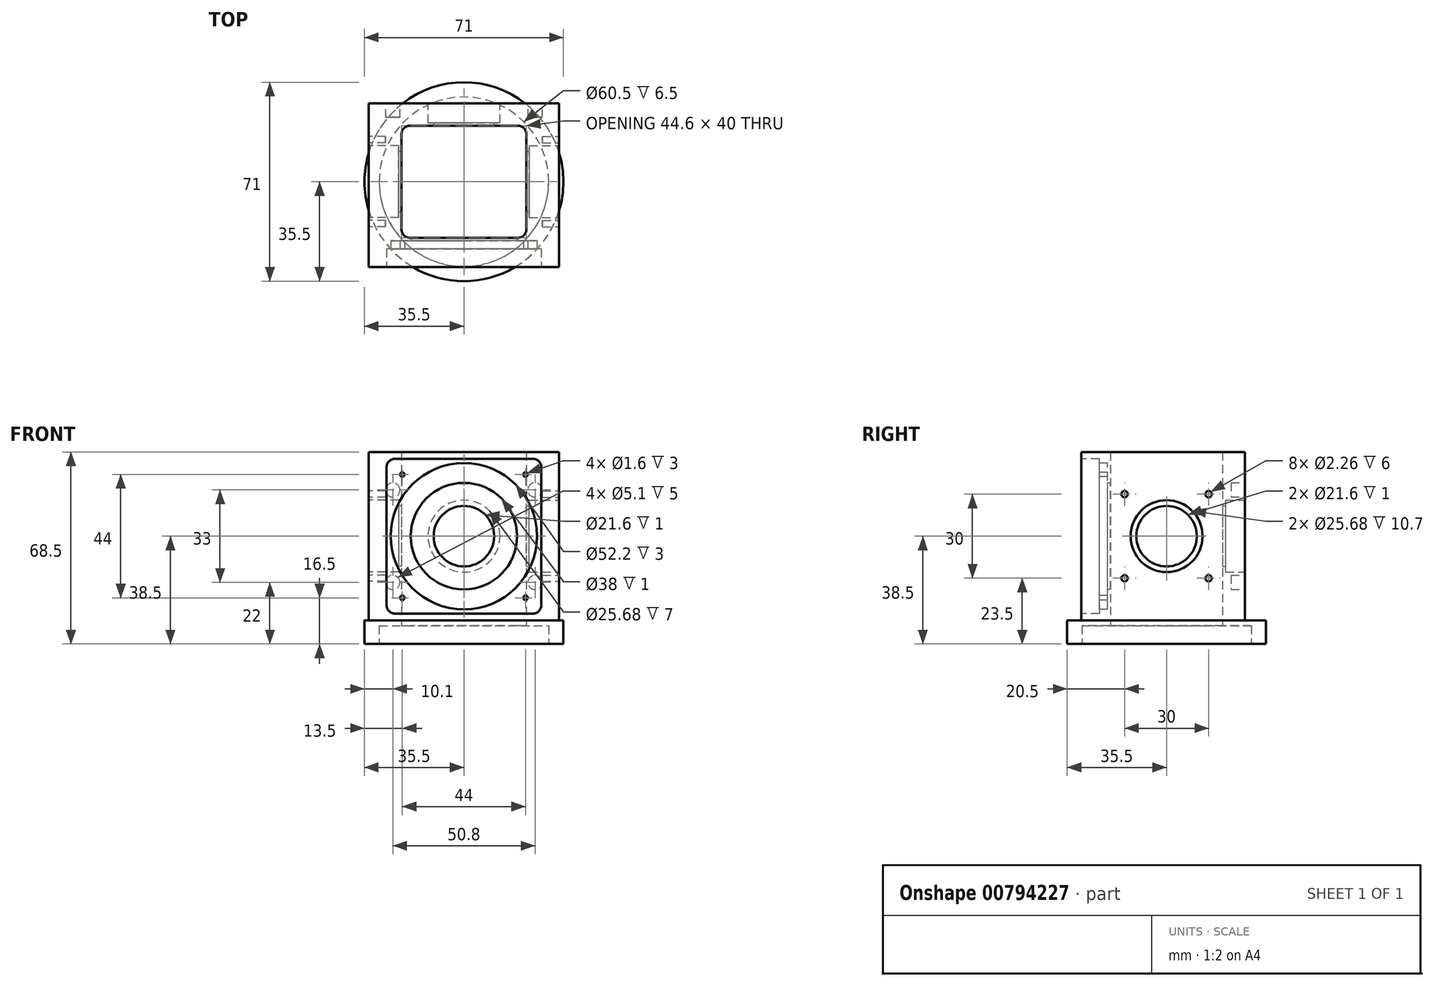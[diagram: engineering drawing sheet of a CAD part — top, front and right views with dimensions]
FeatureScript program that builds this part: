
annotation { "Feature Type Name" : "Feature", "Feature Type Description" : "" }
export const myFeature = defineFeature(function(context is Context, id is Id, definition is map)
    precondition{}
    {
        {
            var Q0;
            Q0=qCreatedBy(makeId("Top.planeOp"),FACE);
            var sketch = newSketch(context, id + "F0", { "sketchPlane" : qUnion([Q0])});
            skCircle(sketch, "E0", {"center": v(0, 0) * mm, "radius": 30.25 * mm});
            skSolve(sketch);
        }
        {
            var Q0;
            Q0=qCreatedBy(makeId("Top.planeOp"),FACE);
            var sketch = newSketch(context, id + "F1", { "sketchPlane" : qUnion([Q0])});
            skCircle(sketch, "E1", {"center": v(0, 0) * mm, "radius": 35.5 * mm});
            skSolve(sketch);
        }
        {
            var Q0;
            Q0=qSketchRegion(id+"F1",true);
            extrude(context, id + "F2", {"entities" : qUnion([Q0]), "depth" : 8.5 * mm, "offsetDistance" : 25 * mm});
        }
        {
            var Q0;
            Q0=qSketchRegion(id+"F0",true);
            extrude(context, id + "F3", {"entities" : qUnion([Q0]), "operationType" : NewBodyOperationType.REMOVE, "depth" : 8.5 * mm, "offsetDistance" : 25 * mm});
        }
        {
            var Q0;
            Q0=makeQuery(id+"F2.opExtrude","CAP_FACE",FACE,{"disambiguationData":[OSD([sQuery(id+"F1.wireOp",EDGE,"E1")])],"isStart":false});
            var sketch = newSketch(context, id + "F4", { "sketchPlane" : qUnion([Q0])});
            skLineSegment(sketch, "E2.bottom", {"start": v(19.3, -20) * mm, "end": v(-19.3, -20) * mm});
            skLineSegment(sketch, "E2.top", {"start": v(19.3, 20) * mm, "end": v(-19.3, 20) * mm});
            skLineSegment(sketch, "E2.left", {"start": v(22.3, -17) * mm, "end": v(22.3, 17) * mm});
            skLineSegment(sketch, "E2.right", {"start": v(-22.3, -17) * mm, "end": v(-22.3, 17) * mm});
            skPoint(sketch, "E2.middle", {"position": v(0, 0) * mm});
            skPoint(sketch, "E3.visualSharp", {"position": v(-22.3, 20) * mm});
            skArc(sketch, "E3.filletArc", {"start": v(-19.3, 20) * mm, "mid": v(-21.42, 19.12) * mm, "end": v(-22.3, 17) * mm});
            skPoint(sketch, "E4.visualSharp", {"position": v(22.3, 20) * mm});
            skArc(sketch, "E4.filletArc", {"start": v(22.3, 17) * mm, "mid": v(21.42, 19.12) * mm, "end": v(19.3, 20) * mm});
            skPoint(sketch, "E5.visualSharp", {"position": v(22.3, -20) * mm});
            skArc(sketch, "E5.filletArc", {"start": v(19.3, -20) * mm, "mid": v(21.42, -19.12) * mm, "end": v(22.3, -17) * mm});
            skPoint(sketch, "E6.visualSharp", {"position": v(-22.3, -20) * mm});
            skArc(sketch, "E6.filletArc", {"start": v(-22.3, -17) * mm, "mid": v(-21.42, -19.12) * mm, "end": v(-19.3, -20) * mm});
            skSolve(sketch);
        }
        {
            var Q0;
            Q0=makeQuery(id+"F4.imprint","IMPRINT",FACE,{"disambiguationData":[TD([[makeQuery(id+"F4.imprint","IMPRINT",EDGE,{"derivedFrom":makeQuery(id+"F2.opExtrude","CAP_EDGE",EDGE,{"disambiguationData":[OSD([sQuery(id+"F1.wireOp",EDGE,"E1")])],"isStart":false})}),1.0]])]});
            var sketch = newSketch(context, id + "F5", { "sketchPlane" : qUnion([Q0])});
            skLineSegment(sketch, "E7.bottom", {"start": v(-34, 0) * mm, "end": v(34, 0) * mm});
            skLineSegment(sketch, "E7.top", {"start": v(-34, 28) * mm, "end": v(34, 28) * mm});
            skLineSegment(sketch, "E7.left", {"start": v(-34, 0) * mm, "end": v(-34, 28) * mm});
            skLineSegment(sketch, "E7.right", {"start": v(34, 0) * mm, "end": v(34, 28) * mm});
            skLineSegment(sketch, "E8.top", {"start": v(-34, -30.5) * mm, "end": v(34, -30.5) * mm});
            skLineSegment(sketch, "E8.left", {"start": v(-34, 0) * mm, "end": v(-34, -30.5) * mm});
            skLineSegment(sketch, "E8.right", {"start": v(34, 0) * mm, "end": v(34, -30.5) * mm});
            skSolve(sketch);
        }
        {
            var Q0;
            Q0=qSketchRegion(id+"F5",true);
            extrude(context, id + "F6", {"entities" : qUnion([Q0]), "operationType" : NewBodyOperationType.ADD, "depth" : 60 * mm, "offsetDistance" : 25 * mm});
        }
        {
            var Q0;
            {var subQ0=makeQuery(id+"F3.boolean.opBoolean","COPY",FACE,{"derivedFrom":makeQuery(id+"F3.opExtrude","SWEPT_FACE",FACE,{"disambiguationData":[OSD([sQuery(id+"F0.wireOp",EDGE,"E0")])]})});var subQ1=sQuery(id+"F4.wireOp",EDGE,"E2.bottom");var subQ2=sQuery(id+"F5.wireOp",EDGE,"E8.left");var subQ3=sQuery(id+"F5.wireOp",EDGE,"E7.left");var subQ4=sQuery(id+"F5.wireOp",EDGE,"E7.top");var subQ5=sQuery(id+"F5.wireOp",EDGE,"E8.right");var subQ6=sQuery(id+"F5.wireOp",EDGE,"E7.right");Q0=makeQuery(id+"F9.boolean.opBoolean","SPLIT",FACE,{"disambiguationData":[TD([makeQuery(id+"F9.opExtrude","SWEPT_FACE",FACE,{"disambiguationData":[OSD([subQ1])]})])],"derivedFrom":makeQuery(id+"F6.boolean.opBoolean","SPLIT",FACE,{"disambiguationData":[TD([makeQuery(id+"F2.opExtrude","CAP_FACE",FACE,{"disambiguationData":[OSD([sQuery(id+"F1.wireOp",EDGE,"E1")])],"isStart":false}),subQ0,makeQuery(id+"F6.opExtrude","SWEPT_FACE",FACE,{"disambiguationData":[OSD([subQ4])]}),makeQuery(id+"F6.opExtrude","SWEPT_FACE",FACE,{"disambiguationData":[OSD([subQ3,subQ2])]}),makeQuery(id+"F6.opExtrude","SWEPT_FACE",FACE,{"disambiguationData":[OSD([subQ6,subQ5])]})])],"derivedFrom":makeQuery(id+"F6.opExtrude","CAP_FACE",FACE,{"disambiguationData":[OSD([subQ4,subQ3,subQ6,sQuery(id+"F5.wireOp",EDGE,"E8.top"),subQ2,subQ5])],"isStart":true})})});}
            var sketch = newSketch(context, id + "F7", { "sketchPlane" : qUnion([Q0])});
            skCircle(sketch, "E9", {"center": v(0, 0) * mm, "radius": 35.25 * mm});
            skSolve(sketch);
        }
        {
            var Q0;
            Q0=qSketchRegion(id+"F7",true);
            extrude(context, id + "F8", {"entities" : qUnion([Q0]), "operationType" : NewBodyOperationType.ADD, "depth" : 2 * mm, "offsetDistance" : 25 * mm});
        }
        {
            var Q0;
            Q0=qSketchRegion(id+"F4",true);
            extrude(context, id + "F9", {"entities" : qUnion([Q0]), "operationType" : NewBodyOperationType.REMOVE, "endBound" : BoundingType.SYMMETRIC, "depth" : 200 * mm, "offsetDistance" : 25 * mm});
        }
        {
            var Q0;
            Q0=makeQuery(id+"F6.opExtrude","SWEPT_FACE",FACE,{"disambiguationData":[OSD([sQuery(id+"F5.wireOp",EDGE,"E8.top")])]});
            var sketch = newSketch(context, id + "F10", { "sketchPlane" : qUnion([Q0])});
            skCircle(sketch, "E10", {"center": v(0, 38.5) * mm, "radius": 19 * mm});
            skSolve(sketch);
        }
        {
            var Q0;
            Q0=qSketchRegion(id+"F10",true);
            extrude(context, id + "F11", {"entities" : qUnion([Q0]), "operationType" : NewBodyOperationType.REMOVE, "oppositeDirection" : true, "depth" : 12 * mm, "offsetDistance" : 25 * mm});
        }
        {
            var Q0;
            Q0=makeQuery(id+"F6.opExtrude","SWEPT_FACE",FACE,{"disambiguationData":[OSD([sQuery(id+"F5.wireOp",EDGE,"E8.top")])]});
            var sketch = newSketch(context, id + "F12", { "sketchPlane" : qUnion([Q0])});
            skCircle(sketch, "E11", {"center": v(0, 38.5) * mm, "radius": 26.1 * mm});
            skSolve(sketch);
        }
        {
            var Q0;
            Q0=qSketchRegion(id+"F12",true);
            extrude(context, id + "F13", {"entities" : qUnion([Q0]), "operationType" : NewBodyOperationType.REMOVE, "oppositeDirection" : true, "depth" : 9.5 * mm, "offsetDistance" : 25 * mm});
        }
        {
            var Q0;
            Q0=makeQuery(id+"F6.opExtrude","SWEPT_FACE",FACE,{"disambiguationData":[OSD([sQuery(id+"F5.wireOp",EDGE,"E8.top")])]});
            var sketch = newSketch(context, id + "F14", { "sketchPlane" : qUnion([Q0])});
            skLineSegment(sketch, "E12.bottom", {"start": v(24.63, 10.88) * mm, "end": v(-24.62, 10.88) * mm});
            skLineSegment(sketch, "E12.top", {"start": v(24.63, 66.13) * mm, "end": v(-24.62, 66.13) * mm});
            skLineSegment(sketch, "E12.left", {"start": v(27.63, 13.88) * mm, "end": v(27.63, 63.13) * mm});
            skLineSegment(sketch, "E12.right", {"start": v(-27.62, 13.88) * mm, "end": v(-27.62, 63.13) * mm});
            skPoint(sketch, "E12.middle", {"position": v(0, 38.5) * mm});
            skPoint(sketch, "E13.visualSharp", {"position": v(-27.62, 66.13) * mm});
            skArc(sketch, "E13.filletArc", {"start": v(-24.62, 66.13) * mm, "mid": v(-26.75, 65.25) * mm, "end": v(-27.62, 63.13) * mm});
            skPoint(sketch, "E14.visualSharp", {"position": v(27.63, 66.13) * mm});
            skArc(sketch, "E14.filletArc", {"start": v(27.63, 63.13) * mm, "mid": v(26.75, 65.25) * mm, "end": v(24.63, 66.13) * mm});
            skPoint(sketch, "E15.visualSharp", {"position": v(27.63, 10.88) * mm});
            skArc(sketch, "E15.filletArc", {"start": v(24.63, 10.88) * mm, "mid": v(26.75, 11.75) * mm, "end": v(27.63, 13.88) * mm});
            skPoint(sketch, "E16.visualSharp", {"position": v(-27.62, 10.88) * mm});
            skArc(sketch, "E16.filletArc", {"start": v(-27.62, 13.88) * mm, "mid": v(-26.75, 11.75) * mm, "end": v(-24.62, 10.88) * mm});
            skSolve(sketch);
        }
        {
            var Q0;
            Q0=qSketchRegion(id+"F14",true);
            extrude(context, id + "F15", {"entities" : qUnion([Q0]), "operationType" : NewBodyOperationType.REMOVE, "oppositeDirection" : true, "depth" : 6.5 * mm, "offsetDistance" : 25 * mm});
        }
        {
            var Q0;
            Q0=makeQuery(id+"F6.opExtrude","SWEPT_FACE",FACE,{"disambiguationData":[OSD([sQuery(id+"F5.wireOp",EDGE,"E7.left"),sQuery(id+"F5.wireOp",EDGE,"E8.left")])]});
            var sketch = newSketch(context, id + "F16", { "sketchPlane" : qUnion([Q0])});
            skLineSegment(sketch, "E17", {"start": v(0, 0) * mm, "end": v(0, 38.5) * mm});
            skPoint(sketch, "E17.endSnap0", {"position": v(0, 8.5) * mm});
            skCircle(sketch, "E18", {"center": v(0, 38.5) * mm, "radius": 10.8 * mm});
            skSolve(sketch);
        }
        {
            var Q0;
            Q0=qSketchRegion(id+"F16",true);
            extrude(context, id + "F17", {"entities" : qUnion([Q0]), "operationType" : NewBodyOperationType.REMOVE, "oppositeDirection" : true, "depth" : 25 * mm, "offsetDistance" : 25 * mm});
        }
        {
            var Q0;
            Q0=makeQuery(id+"F6.opExtrude","SWEPT_FACE",FACE,{"disambiguationData":[OSD([sQuery(id+"F5.wireOp",EDGE,"E7.left"),sQuery(id+"F5.wireOp",EDGE,"E8.left")])]});
            var sketch = newSketch(context, id + "F18", { "sketchPlane" : qUnion([Q0])});
            skCircle(sketch, "E19", {"center": v(0, 38.5) * mm, "radius": 12.84 * mm});
            skSolve(sketch);
        }
        {
            var Q0;
            Q0=qSketchRegion(id+"F18",true);
            extrude(context, id + "F19", {"entities" : qUnion([Q0]), "operationType" : NewBodyOperationType.REMOVE, "oppositeDirection" : true, "depth" : 10.7 * mm, "offsetDistance" : 25 * mm});
        }
        {
            var Q0;
            Q0=makeQuery(id+"F6.opExtrude","SWEPT_FACE",FACE,{"disambiguationData":[OSD([sQuery(id+"F5.wireOp",EDGE,"E7.top")])]});
            var sketch = newSketch(context, id + "F20", { "sketchPlane" : qUnion([Q0])});
            skCircle(sketch, "E20", {"center": v(0, 38.5) * mm, "radius": 10.8 * mm});
            skSolve(sketch);
        }
        {
            var Q0;
            Q0=qSketchRegion(id+"F20",true);
            extrude(context, id + "F21", {"entities" : qUnion([Q0]), "operationType" : NewBodyOperationType.REMOVE, "oppositeDirection" : true, "depth" : 25 * mm, "offsetDistance" : 25 * mm});
        }
        {
            var Q0;
            Q0=makeQuery(id+"F6.opExtrude","SWEPT_FACE",FACE,{"disambiguationData":[OSD([sQuery(id+"F5.wireOp",EDGE,"E7.top")])]});
            var sketch = newSketch(context, id + "F22", { "sketchPlane" : qUnion([Q0])});
            skCircle(sketch, "E21", {"center": v(0, 38.5) * mm, "radius": 12.84 * mm});
            skSolve(sketch);
        }
        {
            var Q0;
            Q0=qSketchRegion(id+"F22",true);
            extrude(context, id + "F23", {"entities" : qUnion([Q0]), "operationType" : NewBodyOperationType.REMOVE, "oppositeDirection" : true, "depth" : 7 * mm, "offsetDistance" : 25 * mm});
        }
        {
            var Q0;
            Q0=makeQuery(id+"F15.boolean.opBoolean","COPY",FACE,{"derivedFrom":makeQuery(id+"F15.opExtrude","CAP_FACE",FACE,{"disambiguationData":[OSD([sQuery(id+"F14.wireOp",EDGE,"E12.bottom"),sQuery(id+"F14.wireOp",EDGE,"E12.top"),sQuery(id+"F14.wireOp",EDGE,"E12.left"),sQuery(id+"F14.wireOp",EDGE,"E12.right"),sQuery(id+"F14.wireOp",EDGE,"E13.filletArc"),sQuery(id+"F14.wireOp",EDGE,"E14.filletArc"),sQuery(id+"F14.wireOp",EDGE,"E15.filletArc"),sQuery(id+"F14.wireOp",EDGE,"E16.filletArc")])],"isStart":false})});
            var sketch = newSketch(context, id + "F24", { "sketchPlane" : qUnion([Q0])});
            skPoint(sketch, "E22.middle", {"position": v(0, 38.5) * mm});
            skCircle(sketch, "E23", {"center": v(-22, 60.5) * mm, "radius": 0.8 * mm});
            skCircle(sketch, "E24", {"center": v(22, 60.5) * mm, "radius": 0.8 * mm});
            skCircle(sketch, "E25", {"center": v(22, 16.5) * mm, "radius": 0.8 * mm});
            skCircle(sketch, "E26", {"center": v(-22, 16.5) * mm, "radius": 0.8 * mm});
            skSolve(sketch);
        }
        {
            var Q0;
            Q0=qSketchRegion(id+"F24",true);
            extrude(context, id + "F25", {"entities" : qUnion([Q0]), "operationType" : NewBodyOperationType.REMOVE, "oppositeDirection" : true, "depth" : 3 * mm, "offsetDistance" : 25 * mm});
        }
        {
            var Q0;
            Q0=makeQuery(id+"F6.opExtrude","SWEPT_FACE",FACE,{"disambiguationData":[OSD([sQuery(id+"F5.wireOp",EDGE,"E7.top")])]});
            var sketch = newSketch(context, id + "F26", { "sketchPlane" : qUnion([Q0])});
            skPoint(sketch, "E27.middle", {"position": v(0, 38.5) * mm});
            skCircle(sketch, "E28", {"center": v(-25.4, 55) * mm, "radius": 2.55 * mm});
            skCircle(sketch, "E29", {"center": v(25.4, 55) * mm, "radius": 2.55 * mm});
            skCircle(sketch, "E30", {"center": v(25.4, 22) * mm, "radius": 2.55 * mm});
            skCircle(sketch, "E31", {"center": v(-25.4, 22) * mm, "radius": 2.55 * mm});
            skSolve(sketch);
        }
        {
            var Q0;
            Q0 = qSketchRegion(id + "F26", true);
            extrude(context, id + "F27", {"entities" : qUnion([Q0]), "operationType" : NewBodyOperationType.REMOVE, "oppositeDirection" : true, "depth" : 5 * mm, "offsetDistance" : 25 * mm});
        }
        {
            var Q0;
            Q0=makeQuery(id+"F6.opExtrude","SWEPT_FACE",FACE,{"disambiguationData":[OSD([sQuery(id+"F5.wireOp",EDGE,"E7.right"),sQuery(id+"F5.wireOp",EDGE,"E8.right")])]});
            var sketch = newSketch(context, id + "F28", { "sketchPlane" : qUnion([Q0])});
            skPoint(sketch, "E32.endSnap0", {"position": v(0, 8.5) * mm});
            skCircle(sketch, "E33", {"center": v(0, 38.5) * mm, "radius": 10.8 * mm});
            skSolve(sketch);
        }
        {
            var Q0;
            Q0 = qSketchRegion(id + "F28", true);
            extrude(context, id + "F29", {"entities" : qUnion([Q0]), "operationType" : NewBodyOperationType.REMOVE, "oppositeDirection" : true, "depth" : 25 * mm, "offsetDistance" : 25 * mm});
        }
        {
            var Q0;
            Q0=makeQuery(id+"F6.opExtrude","SWEPT_FACE",FACE,{"disambiguationData":[OSD([sQuery(id+"F5.wireOp",EDGE,"E7.right"),sQuery(id+"F5.wireOp",EDGE,"E8.right")])]});
            var sketch = newSketch(context, id + "F30", { "sketchPlane" : qUnion([Q0])});
            skCircle(sketch, "E34", {"center": v(0, 38.5) * mm, "radius": 12.84 * mm});
            skSolve(sketch);
        }
        {
            var Q0;
            Q0 = qSketchRegion(id + "F30", true);
            extrude(context, id + "F31", {"entities" : qUnion([Q0]), "operationType" : NewBodyOperationType.REMOVE, "oppositeDirection" : true, "depth" : 10.7 * mm, "offsetDistance" : 25 * mm});
        }
        {
            var Q0;
            Q0=makeQuery(id+"F6.opExtrude","SWEPT_FACE",FACE,{"disambiguationData":[OSD([sQuery(id+"F5.wireOp",EDGE,"E7.right"),sQuery(id+"F5.wireOp",EDGE,"E8.right")])]});
            var sketch = newSketch(context, id + "F32", { "sketchPlane" : qUnion([Q0])});
            skPoint(sketch, "E35.middle", {"position": v(0, 38.5) * mm});
            skCircle(sketch, "E36", {"center": v(-15, 53.5) * mm, "radius": 1.13 * mm});
            skCircle(sketch, "E37", {"center": v(15, 53.5) * mm, "radius": 1.13 * mm});
            skCircle(sketch, "E38", {"center": v(15, 23.5) * mm, "radius": 1.13 * mm});
            skCircle(sketch, "E39", {"center": v(-15, 23.5) * mm, "radius": 1.13 * mm});
            skSolve(sketch);
        }
        {
            var Q0;
            Q0 = qSketchRegion(id + "F32", true);
            extrude(context, id + "F33", {"entities" : qUnion([Q0]), "operationType" : NewBodyOperationType.REMOVE, "oppositeDirection" : true, "depth" : 6 * mm, "offsetDistance" : 25 * mm});
        }
        {
            var Q0;
            Q0=makeQuery(id+"F6.opExtrude","SWEPT_FACE",FACE,{"disambiguationData":[OSD([sQuery(id+"F5.wireOp",EDGE,"E7.left"),sQuery(id+"F5.wireOp",EDGE,"E8.left")])]});
            var sketch = newSketch(context, id + "F34", { "sketchPlane" : qUnion([Q0])});
            skPoint(sketch, "E40.middle", {"position": v(0, 38.5) * mm});
            skCircle(sketch, "E41", {"center": v(-15, 23.5) * mm, "radius": 1.13 * mm});
            skCircle(sketch, "E42", {"center": v(15, 23.5) * mm, "radius": 1.13 * mm});
            skCircle(sketch, "E43", {"center": v(15, 53.5) * mm, "radius": 1.13 * mm});
            skCircle(sketch, "E44", {"center": v(-15, 53.5) * mm, "radius": 1.13 * mm});
            skSolve(sketch);
        }
        {
            var Q0;
            Q0 = qSketchRegion(id + "F34", true);
            extrude(context, id + "F35", {"entities" : qUnion([Q0]), "operationType" : NewBodyOperationType.REMOVE, "oppositeDirection" : true, "depth" : 6 * mm, "offsetDistance" : 25 * mm});
        }
    });
